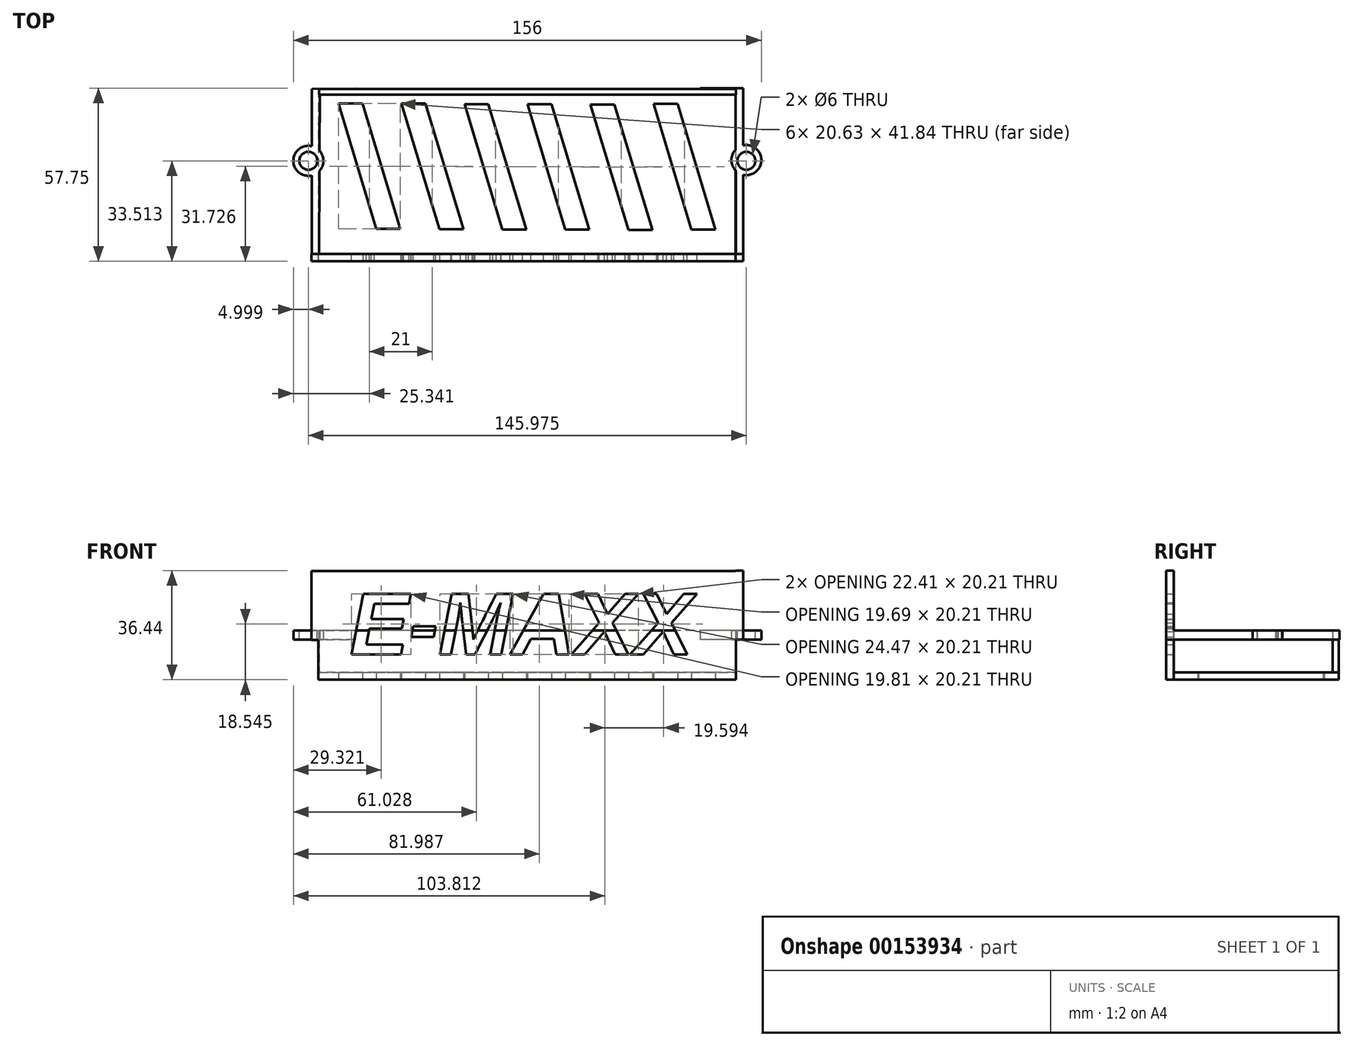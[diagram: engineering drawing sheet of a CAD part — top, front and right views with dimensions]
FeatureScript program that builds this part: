
annotation { "Feature Type Name" : "Feature", "Feature Type Description" : "" }
export const myFeature = defineFeature(function(context is Context, id is Id, definition is map)
    precondition{}
    {
        {
            var Q0;
            Q0=qCreatedBy(makeId("Top.planeOp"),FACE);
            var sketch = newSketch(context, id + "F0", { "sketchPlane" : qUnion([Q0])});
            skLineSegment(sketch, "E0.bottom", {"start": v(-66.08, 29.75) * mm, "end": v(72.92, 29.75) * mm});
            skLineSegment(sketch, "E0.top", {"start": v(-66.08, -25.25) * mm, "end": v(72.92, -25.25) * mm});
            skLineSegment(sketch, "E0.left", {"start": v(-66.08, 29.75) * mm, "end": v(-66.08, -25.25) * mm});
            skLineSegment(sketch, "E0.right", {"start": v(72.92, 29.75) * mm, "end": v(72.92, -25.25) * mm});
            skLineSegment(sketch, "E1", {"start": v(-59.4, 24.9) * mm, "end": v(-51.4, 24.9) * mm});
            skLineSegment(sketch, "E2", {"start": v(-51.4, 24.9) * mm, "end": v(-38.77, -16.94) * mm});
            skLineSegment(sketch, "E3", {"start": v(-38.77, -16.94) * mm, "end": v(-46.77, -16.94) * mm});
            skLineSegment(sketch, "E4", {"start": v(-46.77, -16.94) * mm, "end": v(-59.4, 24.9) * mm});
            skLineSegment(sketch, "E5", {"start": v(-38.4, 24.86) * mm, "end": v(-30.4, 24.86) * mm});
            skLineSegment(sketch, "E6", {"start": v(-30.4, 24.86) * mm, "end": v(-17.77, -16.98) * mm});
            skLineSegment(sketch, "E7", {"start": v(-17.77, -16.98) * mm, "end": v(-25.77, -16.98) * mm});
            skLineSegment(sketch, "E8", {"start": v(-25.77, -16.98) * mm, "end": v(-38.4, 24.86) * mm});
            skLineSegment(sketch, "E9", {"start": v(-17.4, 24.7) * mm, "end": v(-9.4, 24.7) * mm});
            skLineSegment(sketch, "E10", {"start": v(-9.4, 24.7) * mm, "end": v(3.23, -17.15) * mm});
            skLineSegment(sketch, "E11", {"start": v(3.23, -17.15) * mm, "end": v(-4.77, -17.15) * mm});
            skLineSegment(sketch, "E12", {"start": v(-4.77, -17.15) * mm, "end": v(-17.4, 24.7) * mm});
            skLineSegment(sketch, "E13", {"start": v(3.6, 24.7) * mm, "end": v(11.6, 24.7) * mm});
            skLineSegment(sketch, "E14", {"start": v(11.6, 24.7) * mm, "end": v(24.23, -17.15) * mm});
            skLineSegment(sketch, "E15", {"start": v(24.23, -17.15) * mm, "end": v(16.23, -17.15) * mm});
            skLineSegment(sketch, "E16", {"start": v(16.23, -17.15) * mm, "end": v(3.6, 24.7) * mm});
            skLineSegment(sketch, "E17", {"start": v(24.6, 24.57) * mm, "end": v(32.6, 24.57) * mm});
            skLineSegment(sketch, "E18", {"start": v(32.6, 24.57) * mm, "end": v(45.22, -17.28) * mm});
            skLineSegment(sketch, "E19", {"start": v(45.22, -17.28) * mm, "end": v(37.22, -17.28) * mm});
            skLineSegment(sketch, "E20", {"start": v(37.22, -17.28) * mm, "end": v(24.6, 24.57) * mm});
            skLineSegment(sketch, "E21", {"start": v(45.6, 24.72) * mm, "end": v(53.6, 24.72) * mm});
            skLineSegment(sketch, "E22", {"start": v(53.6, 24.72) * mm, "end": v(66.22, -17.12) * mm});
            skLineSegment(sketch, "E23", {"start": v(66.22, -17.12) * mm, "end": v(58.22, -17.12) * mm});
            skLineSegment(sketch, "E24", {"start": v(58.22, -17.12) * mm, "end": v(45.6, 24.72) * mm});
            skSolve(sketch);
        }
        {
            var Q0;
            Q0=makeQuery(id+"F0.imprint","IMPRINT",FACE,{"disambiguationData":[TD([[makeQuery(id+"F0.imprint","IMPRINT",EDGE,{"derivedFrom":sQuery(id+"F0.wireOp",EDGE,"E0.bottom")}),-1.0]])]});
            extrude(context, id + "F1", {"entities" : qUnion([Q0]), "depth" : 2.5 * mm});
        }
        {
            var Q0;
            Q0=makeQuery(id+"F1.opExtrude","SWEPT_FACE",FACE,{"disambiguationData":[OSD([sQuery(id+"F0.wireOp",EDGE,"E0.top")])]});
            var sketch = newSketch(context, id + "F2", { "sketchPlane" : qUnion([Q0])});
            skLineSegment(sketch, "E25.bottom", {"start": v(-66.08, 0) * mm, "end": v(73.12, 0) * mm});
            skLineSegment(sketch, "E25.top", {"start": v(-66.08, 36.3) * mm, "end": v(73.12, 36.3) * mm});
            skLineSegment(sketch, "E25.left", {"start": v(-66.08, 0) * mm, "end": v(-66.08, 36.3) * mm});
            skLineSegment(sketch, "E25.right", {"start": v(73.12, 0) * mm, "end": v(73.12, 36.3) * mm});
            skLineSegment(sketch, "E26.bottom", {"start": v(-65.91, 36.3) * mm, "end": v(-68.41, 36.3) * mm});
            skLineSegment(sketch, "E26.top", {"start": v(-65.91, 13.3) * mm, "end": v(-68.41, 13.3) * mm});
            skLineSegment(sketch, "E26.left", {"start": v(-65.91, 36.3) * mm, "end": v(-65.91, 13.3) * mm});
            skLineSegment(sketch, "E26.right", {"start": v(-68.41, 36.3) * mm, "end": v(-68.41, 13.3) * mm});
            skLineSegment(sketch, "E27.bottom", {"start": v(75.49, 36.44) * mm, "end": v(72.99, 36.44) * mm});
            skLineSegment(sketch, "E27.top", {"start": v(75.49, 13.44) * mm, "end": v(72.99, 13.44) * mm});
            skLineSegment(sketch, "E27.left", {"start": v(75.49, 36.44) * mm, "end": v(75.49, 13.44) * mm});
            skLineSegment(sketch, "E27.right", {"start": v(72.99, 36.44) * mm, "end": v(72.99, 13.44) * mm});
            skText(sketch, "E28", { "text": "E-MAXX", "fontName": "Arimo-BoldItalic.ttf"});
            skPoint(sketch, "E29", {"position": v(9.59, 13.64) * mm});
            skPoint(sketch, "E30", {"position": v(6.62, 13.64) * mm});
            skPoint(sketch, "E31", {"position": v(8.66, 16.6) * mm});
            skPoint(sketch, "E32", {"position": v(10.7, 16.79) * mm});
            const initialGuessF2  = {"E28": [-0.05553, 0.00844, 1, 0, 0.02115]};
            skSetInitialGuess(sketch, initialGuessF2);
            skSolve(sketch);
        }
        {
            var Q0;
            Q0 = qSketchRegion(id + "F2", true);
            extrude(context, id + "F3", {"entities" : qUnion([Q0]), "operationType" : NewBodyOperationType.ADD, "depth" : 2.5 * mm});
        }
        {
            var Q0;
            Q0=makeQuery(id+"F3.opExtrude","SWEPT_FACE",FACE,{"disambiguationData":[OSD([sQuery(id+"F2.wireOp",EDGE,"E27.top")])]});
            var sketch = newSketch(context, id + "F4", { "sketchPlane" : qUnion([Q0])});
            skLineSegment(sketch, "E33", {"start": v(75.49, 27.75) * mm, "end": v(75.49, 25.25) * mm});
            skLineSegment(sketch, "E34", {"start": v(75.49, 25.25) * mm, "end": v(75.49, -30) * mm});
            skLineSegment(sketch, "E35", {"start": v(75.49, -30) * mm, "end": v(61.08, -30) * mm});
            skLineSegment(sketch, "E36", {"start": v(61.08, -30) * mm, "end": v(61.08, -27.9) * mm});
            skLineSegment(sketch, "E37", {"start": v(61.08, -27.9) * mm, "end": v(72.96, -27.9) * mm});
            skLineSegment(sketch, "E38", {"start": v(72.96, -27.9) * mm, "end": v(73.12, 25.25) * mm});
            skLineSegment(sketch, "E39", {"start": v(73.12, 25.25) * mm, "end": v(73.12, 27.75) * mm});
            skLineSegment(sketch, "E40", {"start": v(73.12, 27.75) * mm, "end": v(75.49, 27.75) * mm});
            skLineSegment(sketch, "E41", {"start": v(-68.32, 27.55) * mm, "end": v(-68.17, 27.65) * mm});
            skLineSegment(sketch, "E42", {"start": v(-68.32, 27.55) * mm, "end": v(-68.32, -29.76) * mm});
            skLineSegment(sketch, "E43", {"start": v(-70.84, 27.65) * mm, "end": v(-68.17, 27.65) * mm});
            skLineSegment(sketch, "E44.MirrorCS", {"start": v(-65.8, 27.65) * mm, "end": v(-68.47, 27.65) * mm});
            skLineSegment(sketch, "E45.MirrorCS", {"start": v(-65.8, 25.15) * mm, "end": v(-65.8, 27.65) * mm});
            skLineSegment(sketch, "E46.MirrorCS", {"start": v(-65.64, -27.99) * mm, "end": v(-65.8, 25.15) * mm});
            skLineSegment(sketch, "E47.MirrorCS", {"start": v(-53.76, -27.99) * mm, "end": v(-65.64, -27.99) * mm});
            skLineSegment(sketch, "E48.MirrorCS", {"start": v(-53.76, -29.9) * mm, "end": v(-53.76, -27.99) * mm});
            skLineSegment(sketch, "E49.MirrorCS", {"start": v(-68.32, -29.76) * mm, "end": v(-53.76, -29.9) * mm});
            skLineSegment(sketch, "E50.MirrorCS", {"start": v(-53.76, -27.99) * mm, "end": v(-61.15, -27.99) * mm});
            skCircle(sketch, "E51", {"center": v(-69.43, -5.76) * mm, "radius": 5 * mm});
            skCircle(sketch, "E52", {"center": v(76.57, -6) * mm, "radius": 5 * mm});
            skSolve(sketch);
        }
        {
            var Q0;
            Q0 = qSketchRegion(id + "F4", true);
            extrude(context, id + "F5", {"entities" : qUnion([Q0]), "operationType" : NewBodyOperationType.ADD, "oppositeDirection" : true, "depth" : 3 * mm});
        }
        {
            var Q0;
            Q0=makeQuery(id+"F1.opExtrude","CAP_FACE",FACE,{"disambiguationData":[OSD([sQuery(id+"F0.wireOp",EDGE,"E0.bottom"),sQuery(id+"F0.wireOp",EDGE,"E0.top"),sQuery(id+"F0.wireOp",EDGE,"E0.left"),sQuery(id+"F0.wireOp",EDGE,"E0.right"),sQuery(id+"F0.wireOp",EDGE,"E1"),sQuery(id+"F0.wireOp",EDGE,"E2"),sQuery(id+"F0.wireOp",EDGE,"E3"),sQuery(id+"F0.wireOp",EDGE,"E4"),sQuery(id+"F0.wireOp",EDGE,"E5"),sQuery(id+"F0.wireOp",EDGE,"E6"),sQuery(id+"F0.wireOp",EDGE,"E7"),sQuery(id+"F0.wireOp",EDGE,"E8"),sQuery(id+"F0.wireOp",EDGE,"E9"),sQuery(id+"F0.wireOp",EDGE,"E10"),sQuery(id+"F0.wireOp",EDGE,"E11"),sQuery(id+"F0.wireOp",EDGE,"E12"),sQuery(id+"F0.wireOp",EDGE,"E13"),sQuery(id+"F0.wireOp",EDGE,"E14"),sQuery(id+"F0.wireOp",EDGE,"E15"),sQuery(id+"F0.wireOp",EDGE,"E16"),sQuery(id+"F0.wireOp",EDGE,"E17"),sQuery(id+"F0.wireOp",EDGE,"E18"),sQuery(id+"F0.wireOp",EDGE,"E19"),sQuery(id+"F0.wireOp",EDGE,"E20"),sQuery(id+"F0.wireOp",EDGE,"E21"),sQuery(id+"F0.wireOp",EDGE,"E22"),sQuery(id+"F0.wireOp",EDGE,"E23"),sQuery(id+"F0.wireOp",EDGE,"E24")])],"isStart":false});
            var sketch = newSketch(context, id + "F6", { "sketchPlane" : qUnion([Q0])});
            skLineSegment(sketch, "E53.bottom", {"start": v(73.1, 29.75) * mm, "end": v(-65.9, 29.75) * mm});
            skLineSegment(sketch, "E53.top", {"start": v(73.1, 27.78) * mm, "end": v(-65.9, 27.78) * mm});
            skLineSegment(sketch, "E53.left", {"start": v(73.1, 29.75) * mm, "end": v(73.1, 27.78) * mm});
            skLineSegment(sketch, "E53.right", {"start": v(-65.9, 29.75) * mm, "end": v(-65.9, 27.78) * mm});
            skSolve(sketch);
        }
        {
            var Q0;
            Q0 = qSketchRegion(id + "F6", true);
            extrude(context, id + "F7", {"entities" : qUnion([Q0]), "operationType" : NewBodyOperationType.ADD, "depth" : 14 * mm});
        }
        {
            var Q0;
            Q0=makeQuery(id+"F5.opExtrude","CAP_FACE",FACE,{"disambiguationData":[OSD([sQuery(id+"F4.wireOp",EDGE,"E41"),sQuery(id+"F4.wireOp",EDGE,"E42"),sQuery(id+"F4.wireOp",EDGE,"E44.MirrorCS"),sQuery(id+"F4.wireOp",EDGE,"E45.MirrorCS"),sQuery(id+"F4.wireOp",EDGE,"E46.MirrorCS"),sQuery(id+"F4.wireOp",EDGE,"E49.MirrorCS"),sQuery(id+"F4.wireOp",EDGE,"E47.MirrorCS"),sQuery(id+"F4.wireOp",EDGE,"E50.MirrorCS"),sQuery(id+"F4.wireOp",EDGE,"E48.MirrorCS"),sQuery(id+"F4.wireOp",EDGE,"E51")])],"isStart":false});
            var sketch = newSketch(context, id + "F8", { "sketchPlane" : qUnion([Q0])});
            skPoint(sketch, "E54", {"position": v(-69.43, 5.76) * mm});
            skPoint(sketch, "E55", {"position": v(76.54, 5.76) * mm});
            skSolve(sketch);
        }
        {
            var Q0;
            Q0=sQuery(id+"F8.wireOp",VERTEX,"E54");
            var Q1;
            Q1=sQuery(id+"F8.wireOp",VERTEX,"E55");
            var Q2;
            Q2=makeQuery(id+"F1.opExtrude","SWEPT_BODY",BODY,{"disambiguationData":[OSD([sQuery(id+"F0.wireOp",EDGE,"E0.bottom"),sQuery(id+"F0.wireOp",EDGE,"E0.top"),sQuery(id+"F0.wireOp",EDGE,"E0.left"),sQuery(id+"F0.wireOp",EDGE,"E0.right"),sQuery(id+"F0.wireOp",EDGE,"E1"),sQuery(id+"F0.wireOp",EDGE,"E2"),sQuery(id+"F0.wireOp",EDGE,"E3"),sQuery(id+"F0.wireOp",EDGE,"E4"),sQuery(id+"F0.wireOp",EDGE,"E5"),sQuery(id+"F0.wireOp",EDGE,"E6"),sQuery(id+"F0.wireOp",EDGE,"E7"),sQuery(id+"F0.wireOp",EDGE,"E8"),sQuery(id+"F0.wireOp",EDGE,"E9"),sQuery(id+"F0.wireOp",EDGE,"E10"),sQuery(id+"F0.wireOp",EDGE,"E11"),sQuery(id+"F0.wireOp",EDGE,"E12"),sQuery(id+"F0.wireOp",EDGE,"E13"),sQuery(id+"F0.wireOp",EDGE,"E14"),sQuery(id+"F0.wireOp",EDGE,"E15"),sQuery(id+"F0.wireOp",EDGE,"E16"),sQuery(id+"F0.wireOp",EDGE,"E17"),sQuery(id+"F0.wireOp",EDGE,"E18"),sQuery(id+"F0.wireOp",EDGE,"E19"),sQuery(id+"F0.wireOp",EDGE,"E20"),sQuery(id+"F0.wireOp",EDGE,"E21"),sQuery(id+"F0.wireOp",EDGE,"E22"),sQuery(id+"F0.wireOp",EDGE,"E23"),sQuery(id+"F0.wireOp",EDGE,"E24")])]});
            hole(context, id + "F9", {"style" : HoleStyle.SIMPLE, "endStyle" : HoleEndStyle.THROUGH, "holeDiameter" : 6 * mm, "locations" : qUnion([Q0, Q1]), "scope" : qUnion([Q2]), "isTappedThrough" : true});
        }
    });
